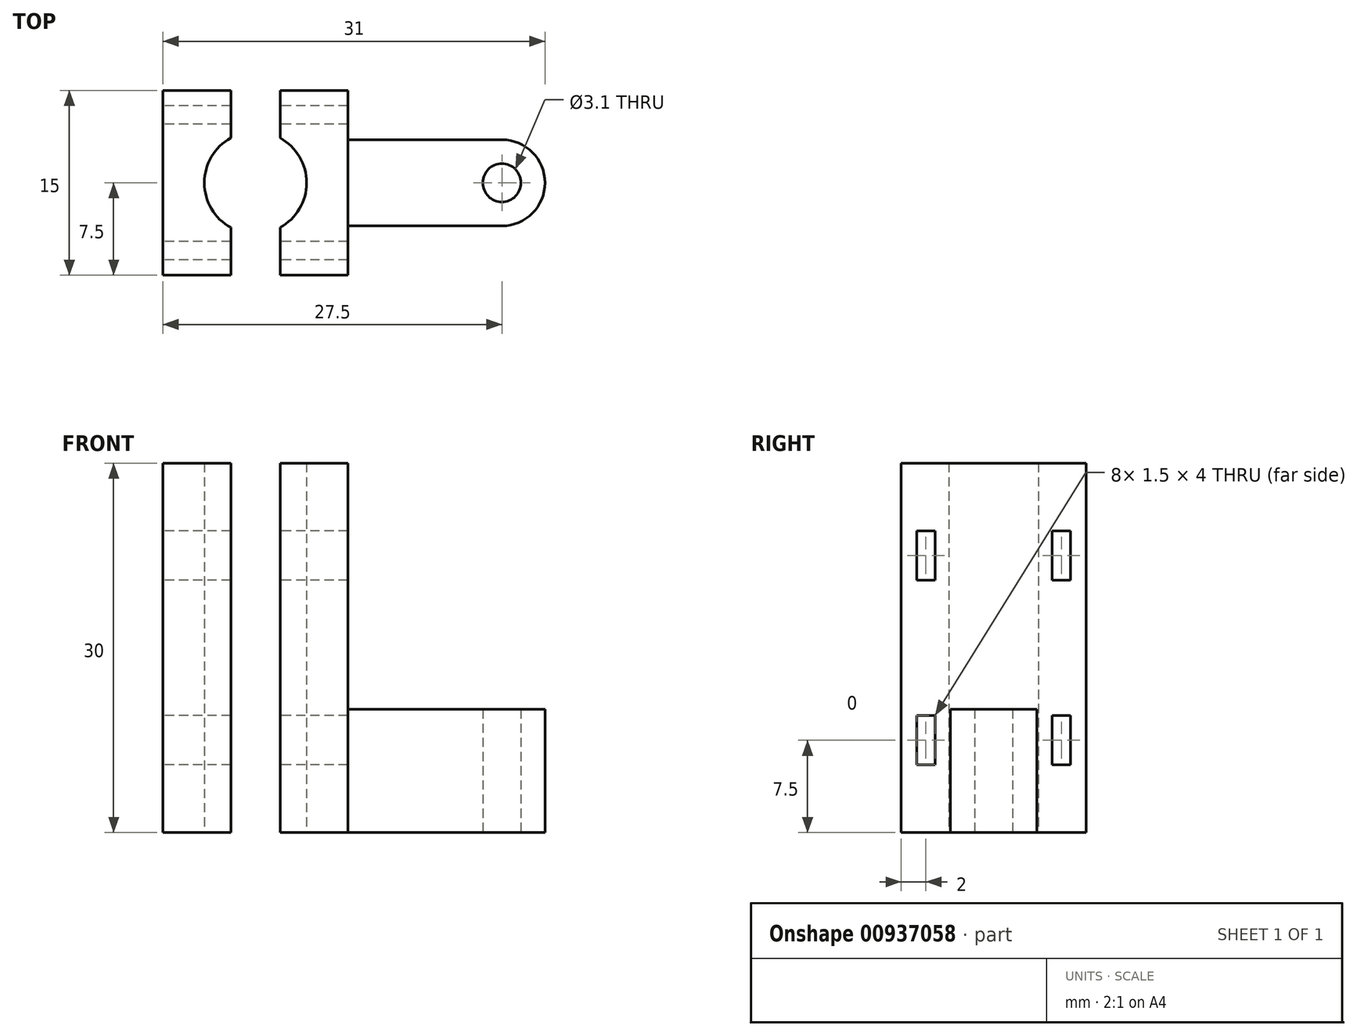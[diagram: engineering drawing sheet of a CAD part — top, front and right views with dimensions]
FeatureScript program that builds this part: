
annotation { "Feature Type Name" : "Feature", "Feature Type Description" : "" }
export const myFeature = defineFeature(function(context is Context, id is Id, definition is map)
    precondition{}
    {
        {
            var Q0;
            Q0=qCreatedBy(makeId("Top.planeOp"),FACE);
            var sketch = newSketch(context, id + "F0", { "sketchPlane" : qUnion([Q0])});
            skCircle(sketch, "E0", {"center": v(0, 0) * mm, "radius": 4.15 * mm});
            skLineSegment(sketch, "E1", {"start": v(0, 0) * mm, "end": v(20, 0) * mm});
            skCircle(sketch, "E2", {"center": v(20, 0) * mm, "radius": 3.5 * mm});
            skLineSegment(sketch, "E3.bottom", {"start": v(-7.5, 7.5) * mm, "end": v(7.5, 7.5) * mm});
            skLineSegment(sketch, "E3.top", {"start": v(-7.5, -7.5) * mm, "end": v(7.5, -7.5) * mm});
            skLineSegment(sketch, "E3.left", {"start": v(-7.5, 7.5) * mm, "end": v(-7.5, -7.5) * mm});
            skLineSegment(sketch, "E3.right", {"start": v(7.5, 7.5) * mm, "end": v(7.5, -7.5) * mm});
            skPoint(sketch, "E4.middle", {"position": v(0, 4.15) * mm});
            skLineSegment(sketch, "E5", {"start": v(-2, 7.5) * mm, "end": v(2, 7.5) * mm});
            skCircle(sketch, "E6", {"center": v(20, 0) * mm, "radius": 1.55 * mm});
            skLineSegment(sketch, "E7", {"start": v(2, 7.5) * mm, "end": v(2, 3.64) * mm});
            skLineSegment(sketch, "E8", {"start": v(-2, 7.5) * mm, "end": v(-2, 3.64) * mm});
            skLineSegment(sketch, "E9", {"start": v(20, 3.5) * mm, "end": v(7.5, 3.5) * mm});
            skLineSegment(sketch, "E10", {"start": v(20, -3.5) * mm, "end": v(7.5, -3.5) * mm});
            skLineSegment(sketch, "E11", {"start": v(-2, -7.5) * mm, "end": v(-2, -3.64) * mm});
            skLineSegment(sketch, "E12", {"start": v(2, -7.5) * mm, "end": v(2, -3.64) * mm});
            skSolve(sketch);
        }
        {
            var Q0;
            {var subQ0=sQuery(id+"F0.wireOp",EDGE,"E3.left");Q0=makeQuery(id+"F0.imprint","IMPRINT",FACE,{"disambiguationData":[TD([[makeQuery(id+"F0.imprint","IMPRINT",EDGE,{"derivedFrom":subQ0}),1.0]])]});}
            var Q1;
            {var subQ3=sQuery(id+"F0.wireOp",EDGE,"E7");Q1=makeQuery(id+"F0.imprint","IMPRINT",FACE,{"disambiguationData":[TD([[makeQuery(id+"F0.imprint","IMPRINT",EDGE,{"derivedFrom":subQ3}),1.0]])]});}
            var Q2;
            {var subQ5=sQuery(id+"F0.wireOp",EDGE,"iRnMnz41-1cGJ-gI2O-KiK1-94zr2ula3uD4");Q2=makeQuery(id+"F0.imprint","IMPRINT",FACE,{"disambiguationData":[TD([[makeQuery(id+"F0.imprint","IMPRINT",EDGE,{"derivedFrom":subQ5}),-1.0]])]});}
            var Q3;
            {var subQ6=sQuery(id+"F0.wireOp",EDGE,"E12");Q3=makeQuery(id+"F0.imprint","IMPRINT",FACE,{"disambiguationData":[TD([[makeQuery(id+"F0.imprint","IMPRINT",EDGE,{"derivedFrom":subQ6}),-1.0]])]});}
            extrude(context, id + "F1", {"entities" : qUnion([Q0, Q1, Q2, Q3]), "depth" : 30 * mm, "offsetDistance" : 25 * mm});
        }
        {
            var Q0;
            Q0=makeQuery(id+"F1.opExtrude","SWEPT_FACE",FACE,{"disambiguationData":[OSD([sQuery(id+"F0.wireOp",EDGE,"E3.left")])]});
            var sketch = newSketch(context, id + "F2", { "sketchPlane" : qUnion([Q0])});
            skLineSegment(sketch, "E13.bottom", {"start": v(-4.75, 9.5) * mm, "end": v(-6.25, 9.5) * mm});
            skLineSegment(sketch, "E13.top", {"start": v(-4.75, 5.5) * mm, "end": v(-6.25, 5.5) * mm});
            skLineSegment(sketch, "E13.left", {"start": v(-4.75, 9.5) * mm, "end": v(-4.75, 5.5) * mm});
            skLineSegment(sketch, "E13.right", {"start": v(-6.25, 9.5) * mm, "end": v(-6.25, 5.5) * mm});
            skPoint(sketch, "E13.middle", {"position": v(-5.5, 7.5) * mm});
            skLineSegment(sketch, "E14.bottom", {"start": v(-4.75, 24.5) * mm, "end": v(-6.25, 24.5) * mm});
            skLineSegment(sketch, "E14.top", {"start": v(-4.75, 20.5) * mm, "end": v(-6.25, 20.5) * mm});
            skLineSegment(sketch, "E14.left", {"start": v(-4.75, 24.5) * mm, "end": v(-4.75, 20.5) * mm});
            skLineSegment(sketch, "E14.right", {"start": v(-6.25, 24.5) * mm, "end": v(-6.25, 20.5) * mm});
            skPoint(sketch, "E14.middle", {"position": v(-5.5, 22.5) * mm});
            skLineSegment(sketch, "E15.MirrorCS", {"start": v(4.75, 9.5) * mm, "end": v(6.25, 9.5) * mm});
            skLineSegment(sketch, "E16.MirrorCS", {"start": v(4.75, 9.5) * mm, "end": v(4.75, 5.5) * mm});
            skPoint(sketch, "E17.MirrorP", {"position": v(5.5, 22.5) * mm});
            skLineSegment(sketch, "E18.MirrorCS", {"start": v(4.75, 24.5) * mm, "end": v(6.25, 24.5) * mm});
            skLineSegment(sketch, "E19.MirrorCS", {"start": v(6.25, 24.5) * mm, "end": v(6.25, 20.5) * mm});
            skPoint(sketch, "E20.MirrorP", {"position": v(5.5, 7.5) * mm});
            skLineSegment(sketch, "E21.MirrorCS", {"start": v(6.25, 9.5) * mm, "end": v(6.25, 5.5) * mm});
            skLineSegment(sketch, "E22.MirrorCS", {"start": v(4.75, 5.5) * mm, "end": v(6.25, 5.5) * mm});
            skLineSegment(sketch, "E23.MirrorCS", {"start": v(4.75, 20.5) * mm, "end": v(6.25, 20.5) * mm});
            skLineSegment(sketch, "E24.MirrorCS", {"start": v(4.75, 24.5) * mm, "end": v(4.75, 20.5) * mm});
            skSolve(sketch);
        }
        {
            var Q0;
            Q0=makeQuery(id+"F2.imprint","IMPRINT",FACE,{"disambiguationData":[TD([[makeQuery(id+"F2.imprint","IMPRINT",EDGE,{"derivedFrom":sQuery(id+"F2.wireOp",EDGE,"E14.bottom")}),1.0]])]});
            var Q1;
            Q1=makeQuery(id+"F2.imprint","IMPRINT",FACE,{"disambiguationData":[TD([[makeQuery(id+"F2.imprint","IMPRINT",EDGE,{"derivedFrom":sQuery(id+"F2.wireOp",EDGE,"E13.bottom")}),1.0]])]});
            var Q2;
            Q2=makeQuery(id+"F2.imprint","IMPRINT",FACE,{"disambiguationData":[TD([[makeQuery(id+"F2.imprint","IMPRINT",EDGE,{"derivedFrom":sQuery(id+"F2.wireOp",EDGE,"E15.MirrorCS")}),-1.0]])]});
            var Q3;
            Q3=makeQuery(id+"F2.imprint","IMPRINT",FACE,{"disambiguationData":[TD([[makeQuery(id+"F2.imprint","IMPRINT",EDGE,{"derivedFrom":sQuery(id+"F2.wireOp",EDGE,"E18.MirrorCS")}),-1.0]])]});
            var Q4;
            Q4=makeQuery(id+"F1.opExtrude","SWEPT_FACE",FACE,{"disambiguationData":[OSD([sQuery(id+"F0.wireOp",EDGE,"E3.right")])]});
            extrude(context, id + "F3", {"entities" : qUnion([Q0, Q1, Q2, Q3]), "operationType" : NewBodyOperationType.REMOVE, "endBound" : BoundingType.UP_TO_SURFACE, "oppositeDirection" : true, "depth" : 25 * mm, "endBoundEntityFace" : qUnion([Q4]), "offsetDistance" : 25 * mm});
        }
        {
            var Q0;
            {var subQ5=sQuery(id+"F0.wireOp",EDGE,"E9");Q0=makeQuery(id+"F0.imprint","IMPRINT",FACE,{"disambiguationData":[TD([[makeQuery(id+"F0.imprint","IMPRINT",EDGE,{"derivedFrom":subQ5}),1.0]])]});}
            var Q1;
            Q1=makeQuery(id+"F0.imprint","IMPRINT",FACE,{"disambiguationData":[TD([[makeQuery(id+"F0.imprint","IMPRINT",EDGE,{"derivedFrom":sQuery(id+"F0.wireOp",EDGE,"E6")}),-1.0]])]});
            var Q2;
            {var subQ5=sQuery(id+"F0.wireOp",EDGE,"dBmPXZuu-KlFU-QEZ2-Boxh-zn3ukYOreCOM");Q2=makeQuery(id+"F0.imprint","IMPRINT",FACE,{"disambiguationData":[TD([[makeQuery(id+"F0.imprint","IMPRINT",EDGE,{"derivedFrom":subQ5}),1.0]])]});}
            var Q3;
            {var subQ5=sQuery(id+"F0.wireOp",EDGE,"E10");Q3=makeQuery(id+"F0.imprint","IMPRINT",FACE,{"disambiguationData":[TD([[makeQuery(id+"F0.imprint","IMPRINT",EDGE,{"derivedFrom":subQ5}),-1.0]])]});}
            extrude(context, id + "F4", {"entities" : qUnion([Q0, Q1, Q2, Q3]), "operationType" : NewBodyOperationType.ADD, "depth" : 10 * mm, "offsetDistance" : 25 * mm});
        }
    });
